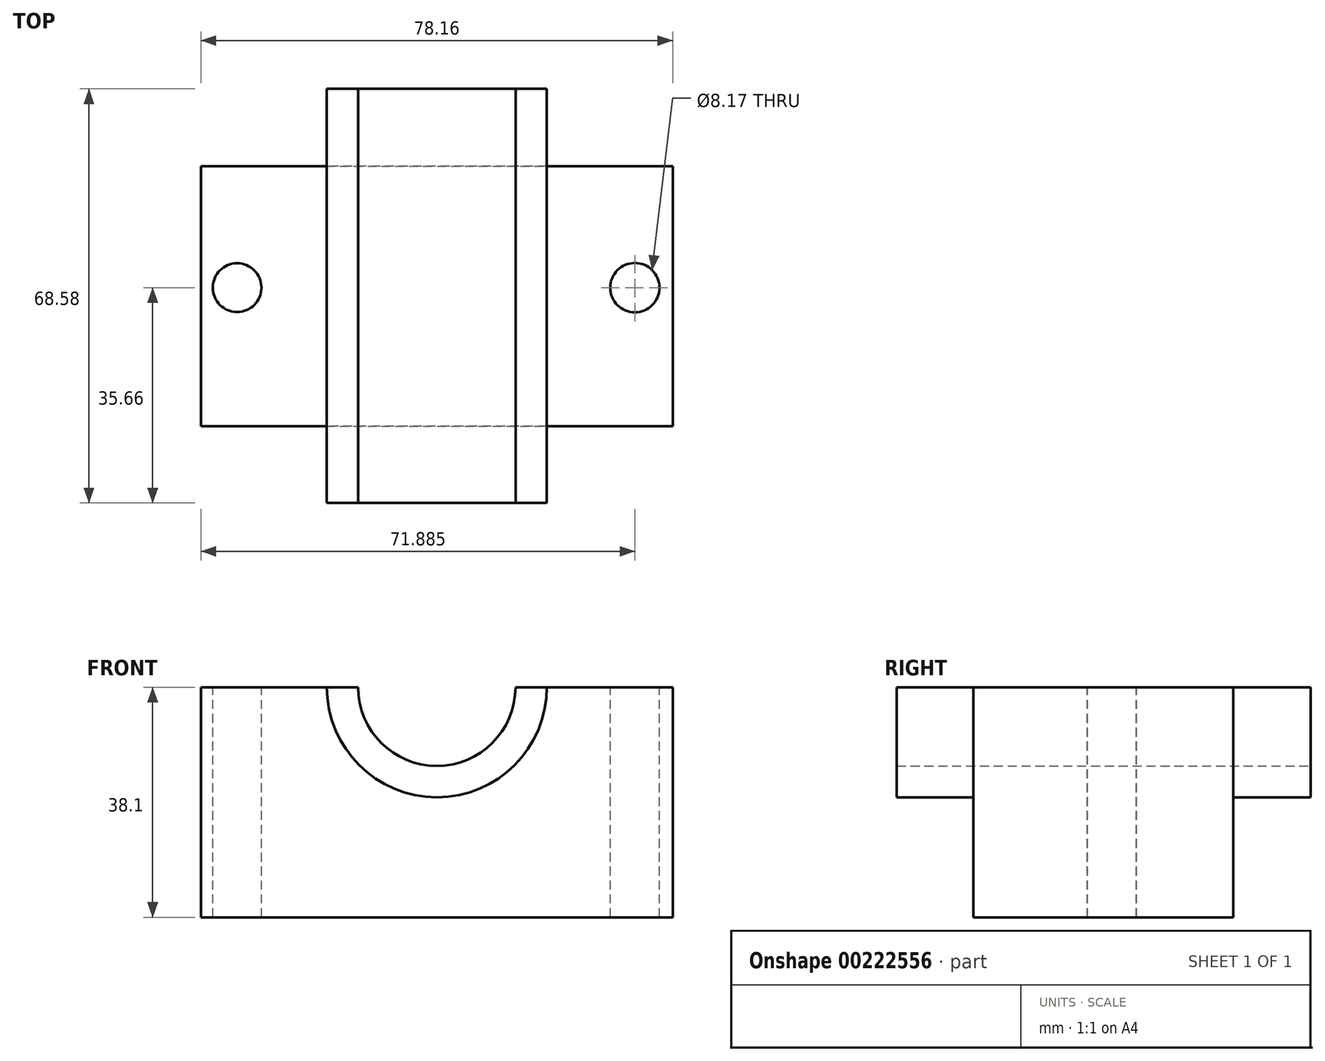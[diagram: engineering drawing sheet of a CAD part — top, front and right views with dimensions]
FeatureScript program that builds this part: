
annotation { "Feature Type Name" : "Feature", "Feature Type Description" : "" }
export const myFeature = defineFeature(function(context is Context, id is Id, definition is map)
    precondition{}
    {
        {
            var Q0;
            Q0=qCreatedBy(makeId("Top.planeOp"),FACE);
            var sketch = newSketch(context, id + "F0", { "sketchPlane" : qUnion([Q0])});
            skLineSegment(sketch, "E0.bottom", {"start": v(-36.8, 20.1) * mm, "end": v(41.36, 20.1) * mm});
            skLineSegment(sketch, "E0.top", {"start": v(-36.8, -22.96) * mm, "end": v(41.36, -22.96) * mm});
            skLineSegment(sketch, "E0.left", {"start": v(-36.8, 20.1) * mm, "end": v(-36.8, -22.96) * mm});
            skLineSegment(sketch, "E0.right", {"start": v(41.36, 20.1) * mm, "end": v(41.36, -22.96) * mm});
            skSolve(sketch);
        }
        {
            var Q0;
            Q0 = qSketchRegion(id + "F0", true);
            extrude(context, id + "F1", {"entities" : qUnion([Q0]), "depth" : 38.1 * mm});
        }
        {
            var Q0;
            Q0=makeQuery(id+"F1.opExtrude","SWEPT_FACE",FACE,{"disambiguationData":[OSD([sQuery(id+"F0.wireOp",EDGE,"E0.top")])]});
            var sketch = newSketch(context, id + "F2", { "sketchPlane" : qUnion([Q0])});
            skCircle(sketch, "E1", {"center": v(2.28, 38.1) * mm, "radius": 18.22 * mm});
            skSolve(sketch);
        }
        {
            var Q0;
            Q0 = qSketchRegion(id + "F2", true);
            extrude(context, id + "F3", {"entities" : qUnion([Q0]), "operationType" : NewBodyOperationType.ADD, "oppositeDirection" : true, "depth" : 55.88 * mm, "hasSecondDirection" : true, "secondDirectionOppositeDirection" : false, "secondDirectionDepth" : 12.7 * mm});
        }
        {
            var Q0;
            Q0=makeQuery(id+"F3.opExtrude","CAP_FACE",FACE,{"disambiguationData":[OSD([sQuery(id+"F2.wireOp",EDGE,"E1")])],"isStart":false});
            var sketch = newSketch(context, id + "F4", { "sketchPlane" : qUnion([Q0])});
            skCircle(sketch, "E2", {"center": v(-2.28, 38.1) * mm, "radius": 13.03 * mm});
            skLineSegment(sketch, "E3", {"start": v(-17.18, 48.59) * mm, "end": v(12.62, 48.59) * mm});
            skArc(sketch, "E4", {"start": v(12.62, 48.59) * mm, "mid": v(-2.28, 77.3) * mm, "end": v(-17.18, 48.59) * mm});
            skSolve(sketch);
        }
        {
            var Q0;
            Q0 = qSketchRegion(id + "F4", true);
            extrude(context, id + "F5", {"entities" : qUnion([Q0]), "operationType" : NewBodyOperationType.REMOVE, "endBound" : BoundingType.THROUGH_ALL, "oppositeDirection" : true, "depth" : 25.4 * mm});
        }
        {
            var Q0;
            Q0=makeQuery(id+"F3.opExtrude","CAP_FACE",FACE,{"disambiguationData":[OSD([sQuery(id+"F2.wireOp",EDGE,"E1")])],"isStart":false});
            var sketch = newSketch(context, id + "F6", { "sketchPlane" : qUnion([Q0])});
            skLineSegment(sketch, "E5", {"start": v(-20.5, 38.07) * mm, "end": v(15.94, 38.07) * mm});
            skArc(sketch, "E6", {"start": v(15.94, 38.07) * mm, "mid": v(-2.28, 57) * mm, "end": v(-20.5, 38.07) * mm});
            skSolve(sketch);
        }
        {
            var Q0;
            Q0 = qSketchRegion(id + "F6", true);
            extrude(context, id + "F7", {"entities" : qUnion([Q0]), "operationType" : NewBodyOperationType.REMOVE, "endBound" : BoundingType.THROUGH_ALL, "oppositeDirection" : true, "depth" : 25.4 * mm});
        }
        {
            var Q0;
            {var subQ0=sQuery(id+"F0.wireOp",EDGE,"E0.bottom");var subQ1=sQuery(id+"F0.wireOp",EDGE,"E0.top");var subQ2=sQuery(id+"F0.wireOp",EDGE,"E0.right");Q0=makeQuery(id+"F3.boolean.opBoolean","SPLIT",FACE,{"disambiguationData":[TD([makeQuery(id+"F1.opExtrude","SWEPT_FACE",FACE,{"disambiguationData":[OSD([subQ2])]})])],"derivedFrom":makeQuery(id+"F1.opExtrude","CAP_FACE",FACE,{"disambiguationData":[OSD([subQ0,subQ1,sQuery(id+"F0.wireOp",EDGE,"E0.left"),subQ2])],"isStart":false})});}
            var sketch = newSketch(context, id + "F8", { "sketchPlane" : qUnion([Q0])});
            skCircle(sketch, "E7", {"center": v(35.08, 0) * mm, "radius": 4.08 * mm});
            skCircle(sketch, "E8", {"center": v(-30.8, 0) * mm, "radius": 4.03 * mm});
            skSolve(sketch);
        }
        {
            var Q0;
            Q0 = qSketchRegion(id + "F8", true);
            extrude(context, id + "F9", {"entities" : qUnion([Q0]), "operationType" : NewBodyOperationType.REMOVE, "endBound" : BoundingType.THROUGH_ALL, "oppositeDirection" : true, "depth" : 25.4 * mm});
        }
    });
